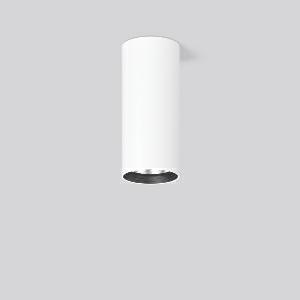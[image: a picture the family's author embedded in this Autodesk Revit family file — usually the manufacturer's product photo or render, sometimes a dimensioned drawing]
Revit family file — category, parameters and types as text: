
# Revit family: heledon_mini_a_931208_002_76_01ce
name_source: partatom
category: Lighting Fixtures
units: mm (PartAtom-declared; Revit-internal decimal feet)

## family parameters
Cut with Voids When Loaded = No
Host = Face
Light Source = No
Part Type = Normal
Room Calculation Point = No
Round Connector Dimension = Use Diameter
Shared = No

## types (1)
- HELEDON mini A (1 x LED Modul 930, 3550 lm, 3000)
    Apparent Load = 29 VA
    Approval mark = CE
    CIE Flux Codes = 100 100 100 100 100
    Color Rendering = 90
    Color Temperature = 3000
    Default Elevation = 1800 mm
    Description = Series: HELEDON mini
Cylindrical surface-mounted downlight. Housing: die-cast aluminium, powder-coated. Internal ceiling frame polycarbonate with bayonet mounting. Black plastic ring and recessed LED to prevent glare from the side. Optical assembly with reflector made of MIRO-Silver with 98% total light reflection for outstanding efficiency - can be changed without tools. Best colour rendering index Ra>90. Suitable for Ceiling mounting. Easy installation with a separate ceiling frame with bayonet mounting and plug connection. Driver integrated. Connected via plug-in connector. High quality converter without flickering and stroboscopic effect. The following accessories can be mounted without use of tools: interchangeable lenses, decorative glasses, honeycomb louvre, clear and frosted diffusers, white interchangeable plastic ring. 
Colour: traffic white, matt (RAL 9016)
Diameter: 87 mm
Height: 197 mm
Lamp: LED
Socket: without socket
Colour temperature: 3000K
Colour rendering index (CRI): 92
System power: 29 W
Rated luminous flux: 3550 lm
Luminous efficiency: 122 lm/W
Control gear: Converter, dimmable, DALI
Protection class: I
Type of protection: IP 20
    Height = 197 mm
    Lamp = 1 x LED Modul 930
    Lamp Light Flux = 3550 lm
    Lamp count = 1
    Length = 87 mm
    Lifetime = 50000 h
    Luminous efficacy = 122 lm/W
    Manufacturer = RZB
    ModVariant = No
    Model = 931208.002.76
    Mounting Place = Ceiling
    Mounting Type = Surface mounted
    Number of Poles = 1
    OnlyDefault = Yes
    Power Factor = 1
    Product Name = HELEDON mini A
    Product group = Surface mounted downlights
    ProductGroupID = 302
    Protection Class = Protection class I
    Protection Degree = IP 20
    RLX_Detail_Level = 1
    RLX_Emergency_Light_Flux = 0 lm
    RLX_Emergency_Type = 0
    RLX_Emergency_Type_DB = No
    RlxData = <blob elided: 106549 chars, md5=b3b9ed98>
    Socket = socket
    Standby Power = 0 W
    System Light Flux = 3550 lm
    System Power = 29 W
    Type Comments = Product without accessories
    Type Image = 931188.002.jpg
    URL = http://relux.com
    VarID = ---
    Voltage = 230 V
    Voltage Range = 220-240 V
    Weight = 0.00 kg
    Width = 0 mm  [stored 0 ft]

note: [stored X ft] marks values corroborated as IEEE doubles in the binary element streams (Revit-internal decimal feet)

## geometry (parser evidence)
native form markers: Blend x4, Sweep x11
no freeform markers — native parametric forms only
